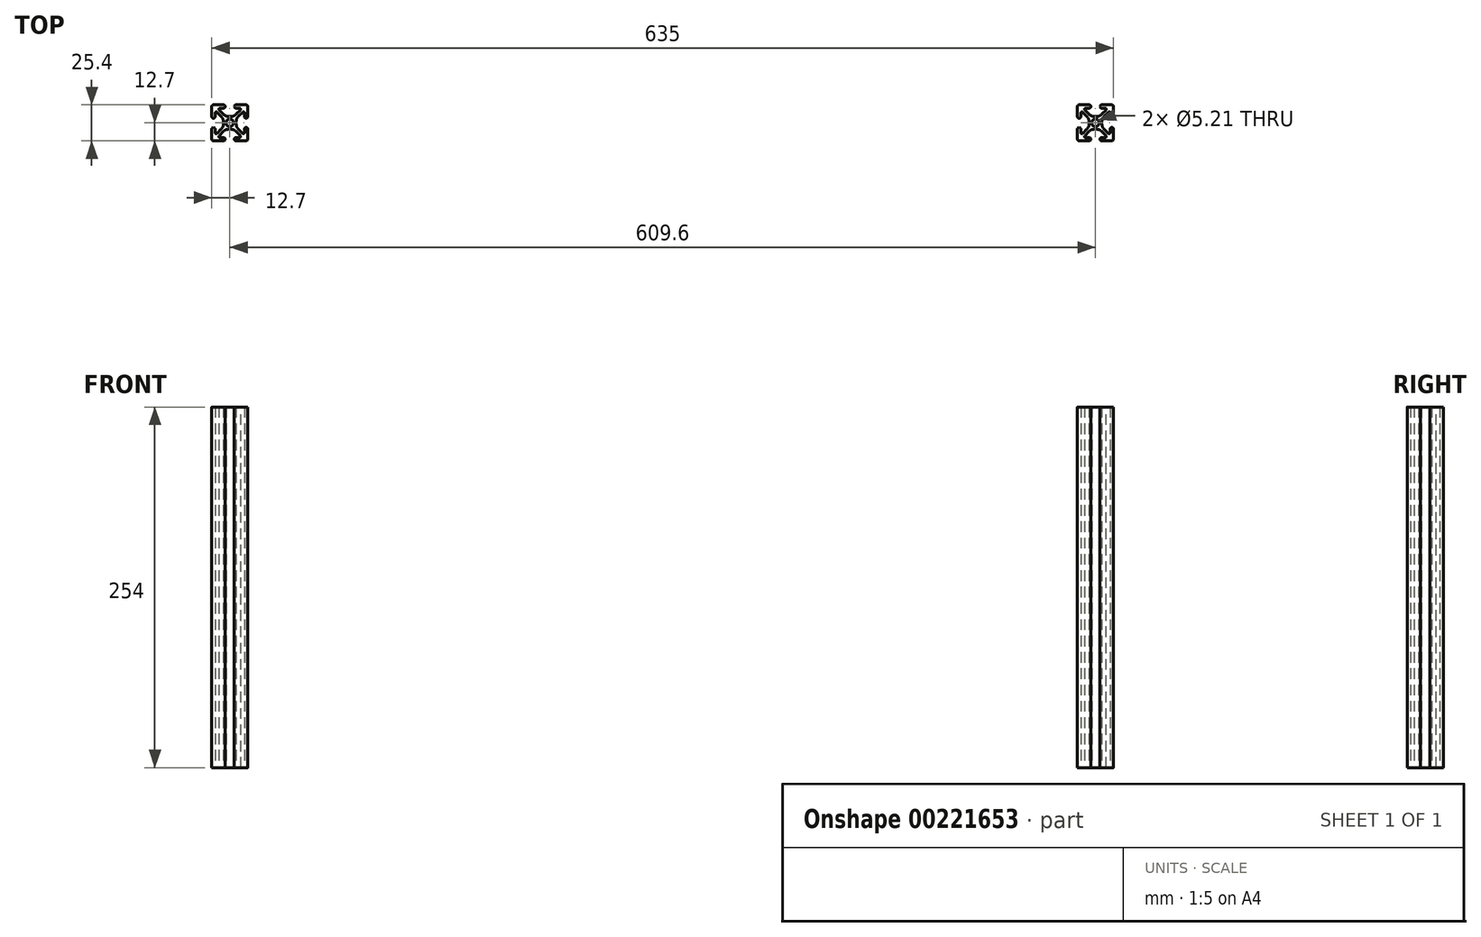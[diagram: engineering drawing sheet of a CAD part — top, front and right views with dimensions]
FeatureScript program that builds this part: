
annotation { "Feature Type Name" : "Feature", "Feature Type Description" : "" }
export const myFeature = defineFeature(function(context is Context, id is Id, definition is map)
    precondition{}
    {
        {
            var Q0;
            Q0=qCreatedBy(makeId("Top.planeOp"),FACE);
            var sketch = newSketch(context, id + "F0", { "sketchPlane" : qUnion([Q0])});
            skLineSegment(sketch, "E0.bottom", {"start": v(12.7, 12.7) * mm, "end": v(-12.7, 12.7) * mm});
            skLineSegment(sketch, "E0.top", {"start": v(12.7, -12.7) * mm, "end": v(-12.7, -12.7) * mm});
            skLineSegment(sketch, "E0.left", {"start": v(12.7, 12.7) * mm, "end": v(12.7, -12.7) * mm});
            skLineSegment(sketch, "E0.right", {"start": v(-12.7, 12.7) * mm, "end": v(-12.7, -12.7) * mm});
            skPoint(sketch, "E0.middle", {"position": v(0, 0) * mm});
            skCircle(sketch, "E1", {"center": v(0, 0) * mm, "radius": 2.6 * mm});
            skLineSegment(sketch, "E2", {"start": v(-12.7, 12.7) * mm, "end": v(12.7, -12.7) * mm, "construction": true});
            skLineSegment(sketch, "E3", {"start": v(0, 12.7) * mm, "end": v(0, -12.7) * mm, "construction": true});
            skLineSegment(sketch, "E4", {"start": v(-12.7, -12.7) * mm, "end": v(12.7, 12.7) * mm, "construction": true});
            skLineSegment(sketch, "E5", {"start": v(-8.78, 10.34) * mm, "end": v(-2.95, 4.5) * mm});
            skLineSegment(sketch, "E6.MirrorCS", {"start": v(8.78, 10.34) * mm, "end": v(2.95, 4.5) * mm});
            skLineSegment(sketch, "E7", {"start": v(-2.95, 4.5) * mm, "end": v(2.95, 4.5) * mm});
            skLineSegment(sketch, "E8.bottom", {"start": v(-3.24, 14.9) * mm, "end": v(3.24, 14.9) * mm});
            skLineSegment(sketch, "E8.left", {"start": v(-3.24, 14.9) * mm, "end": v(-3.24, 10.34) * mm});
            skLineSegment(sketch, "E8.right", {"start": v(3.24, 14.9) * mm, "end": v(3.24, 10.34) * mm});
            skLineSegment(sketch, "E9", {"start": v(-8.78, 10.34) * mm, "end": v(-3.24, 10.34) * mm});
            skLineSegment(sketch, "E10", {"start": v(3.24, 10.34) * mm, "end": v(8.78, 10.34) * mm});
            skLineSegment(sketch, "E11.MirrorCS", {"start": v(-10.34, 8.78) * mm, "end": v(-4.5, 2.95) * mm});
            skLineSegment(sketch, "E12.MirrorCS", {"start": v(-10.34, 8.78) * mm, "end": v(-10.34, 3.24) * mm});
            skLineSegment(sketch, "E13.MirrorCS", {"start": v(-14.9, 3.24) * mm, "end": v(-10.34, 3.24) * mm});
            skLineSegment(sketch, "E14.MirrorCS", {"start": v(-14.9, 3.24) * mm, "end": v(-14.9, -3.24) * mm});
            skLineSegment(sketch, "E15.MirrorCS", {"start": v(-14.9, -3.24) * mm, "end": v(-10.34, -3.24) * mm});
            skLineSegment(sketch, "E16.MirrorCS", {"start": v(-10.34, -3.24) * mm, "end": v(-10.34, -8.78) * mm});
            skLineSegment(sketch, "E17.MirrorCS", {"start": v(-10.34, -8.78) * mm, "end": v(-4.5, -2.95) * mm});
            skLineSegment(sketch, "E18.MirrorCS", {"start": v(-4.5, 2.95) * mm, "end": v(-4.5, -2.95) * mm});
            skLineSegment(sketch, "E19.MirrorCS", {"start": v(10.34, 8.78) * mm, "end": v(4.5, 2.95) * mm});
            skLineSegment(sketch, "E20.MirrorCS", {"start": v(4.5, -2.95) * mm, "end": v(4.5, 2.95) * mm});
            skLineSegment(sketch, "E21.MirrorCS", {"start": v(10.34, -8.78) * mm, "end": v(4.5, -2.95) * mm});
            skLineSegment(sketch, "E22.MirrorCS", {"start": v(10.34, -8.78) * mm, "end": v(10.34, -3.24) * mm});
            skLineSegment(sketch, "E23.MirrorCS", {"start": v(14.9, -3.24) * mm, "end": v(10.34, -3.24) * mm});
            skLineSegment(sketch, "E24.MirrorCS", {"start": v(14.9, -3.24) * mm, "end": v(14.9, 3.24) * mm});
            skLineSegment(sketch, "E25.MirrorCS", {"start": v(14.9, 3.24) * mm, "end": v(10.34, 3.24) * mm});
            skLineSegment(sketch, "E26.MirrorCS", {"start": v(10.34, 3.24) * mm, "end": v(10.34, 8.78) * mm});
            skLineSegment(sketch, "E27", {"start": v(-12.7, 0) * mm, "end": v(12.7, 0) * mm, "construction": true});
            skLineSegment(sketch, "E28.MirrorCS", {"start": v(-8.78, -10.34) * mm, "end": v(-2.95, -4.5) * mm});
            skLineSegment(sketch, "E29.MirrorCS", {"start": v(-8.78, -10.34) * mm, "end": v(-3.24, -10.34) * mm});
            skLineSegment(sketch, "E30.MirrorCS", {"start": v(-3.24, -14.9) * mm, "end": v(-3.24, -10.34) * mm});
            skLineSegment(sketch, "E31.MirrorCS", {"start": v(-3.24, -14.9) * mm, "end": v(3.24, -14.9) * mm});
            skLineSegment(sketch, "E32.MirrorCS", {"start": v(3.24, -14.9) * mm, "end": v(3.24, -10.34) * mm});
            skLineSegment(sketch, "E33.MirrorCS", {"start": v(3.24, -10.34) * mm, "end": v(8.78, -10.34) * mm});
            skLineSegment(sketch, "E34.MirrorCS", {"start": v(8.78, -10.34) * mm, "end": v(2.95, -4.5) * mm});
            skLineSegment(sketch, "E35.MirrorCS", {"start": v(-2.95, -4.5) * mm, "end": v(2.95, -4.5) * mm});
            skSolve(sketch);
        }
        {
            var Q0;
            Q0=makeQuery(id+"F0.imprint","IMPRINT",FACE,{"disambiguationData":[TD([[makeQuery(id+"F0.imprint","IMPRINT",EDGE,{"derivedFrom":sQuery(id+"F0.wireOp",EDGE,"E1")}),-1.0]])]});
            extrude(context, id + "F1", {"entities" : qUnion([Q0]), "depth" : 254 * mm});
        }
        {
            var Q0;
            Q0=makeQuery(id+"F1.opExtrude","SWEPT_EDGE",EDGE,{"disambiguationData":[OSD([sQuery(id+"F0.wireOp",EDGE,"E0.bottom"),sQuery(id+"F0.wireOp",EDGE,"E8.right")])]});
            var Q1;
            Q1=makeQuery(id+"F1.opExtrude","SWEPT_EDGE",EDGE,{"disambiguationData":[OSD([sQuery(id+"F0.wireOp",EDGE,"E8.right"),sQuery(id+"F0.wireOp",EDGE,"E10")])]});
            var Q2;
            Q2=makeQuery(id+"F1.opExtrude","SWEPT_EDGE",EDGE,{"disambiguationData":[OSD([sQuery(id+"F0.wireOp",EDGE,"E0.bottom"),sQuery(id+"F0.wireOp",EDGE,"E8.left")])]});
            var Q3;
            Q3=makeQuery(id+"F1.opExtrude","SWEPT_EDGE",EDGE,{"disambiguationData":[OSD([sQuery(id+"F0.wireOp",EDGE,"E0.right"),sQuery(id+"F0.wireOp",EDGE,"E13.MirrorCS")])]});
            var Q4;
            Q4=makeQuery(id+"F1.opExtrude","SWEPT_EDGE",EDGE,{"disambiguationData":[OSD([sQuery(id+"F0.wireOp",EDGE,"E8.left"),sQuery(id+"F0.wireOp",EDGE,"E9")])]});
            var Q5;
            Q5=makeQuery(id+"F1.opExtrude","SWEPT_EDGE",EDGE,{"disambiguationData":[OSD([sQuery(id+"F0.wireOp",EDGE,"E12.MirrorCS"),sQuery(id+"F0.wireOp",EDGE,"E13.MirrorCS")])]});
            var Q6;
            Q6=makeQuery(id+"F1.opExtrude","SWEPT_EDGE",EDGE,{"disambiguationData":[OSD([sQuery(id+"F0.wireOp",EDGE,"E0.left"),sQuery(id+"F0.wireOp",EDGE,"E25.MirrorCS")])]});
            var Q7;
            Q7=makeQuery(id+"F1.opExtrude","SWEPT_EDGE",EDGE,{"disambiguationData":[OSD([sQuery(id+"F0.wireOp",EDGE,"E25.MirrorCS"),sQuery(id+"F0.wireOp",EDGE,"E26.MirrorCS")])]});
            var Q8;
            Q8=makeQuery(id+"F1.opExtrude","SWEPT_EDGE",EDGE,{"disambiguationData":[OSD([sQuery(id+"F0.wireOp",EDGE,"E0.left"),sQuery(id+"F0.wireOp",EDGE,"E23.MirrorCS")])]});
            var Q9;
            Q9=makeQuery(id+"F1.opExtrude","SWEPT_EDGE",EDGE,{"disambiguationData":[OSD([sQuery(id+"F0.wireOp",EDGE,"E22.MirrorCS"),sQuery(id+"F0.wireOp",EDGE,"E23.MirrorCS")])]});
            var Q10;
            Q10=makeQuery(id+"F1.opExtrude","SWEPT_EDGE",EDGE,{"disambiguationData":[OSD([sQuery(id+"F0.wireOp",EDGE,"E32.MirrorCS"),sQuery(id+"F0.wireOp",EDGE,"E33.MirrorCS")])]});
            var Q11;
            Q11=makeQuery(id+"F1.opExtrude","SWEPT_EDGE",EDGE,{"disambiguationData":[OSD([sQuery(id+"F0.wireOp",EDGE,"E29.MirrorCS"),sQuery(id+"F0.wireOp",EDGE,"E30.MirrorCS")])]});
            var Q12;
            Q12=makeQuery(id+"F1.opExtrude","SWEPT_EDGE",EDGE,{"disambiguationData":[OSD([sQuery(id+"F0.wireOp",EDGE,"E15.MirrorCS"),sQuery(id+"F0.wireOp",EDGE,"E16.MirrorCS")])]});
            var Q13;
            Q13=makeQuery(id+"F1.opExtrude","SWEPT_EDGE",EDGE,{"disambiguationData":[OSD([sQuery(id+"F0.wireOp",EDGE,"E0.right"),sQuery(id+"F0.wireOp",EDGE,"E15.MirrorCS")])]});
            var Q14;
            Q14=makeQuery(id+"F1.opExtrude","SWEPT_EDGE",EDGE,{"disambiguationData":[OSD([sQuery(id+"F0.wireOp",EDGE,"E0.top"),sQuery(id+"F0.wireOp",EDGE,"E30.MirrorCS")])]});
            var Q15;
            Q15=makeQuery(id+"F1.opExtrude","SWEPT_EDGE",EDGE,{"disambiguationData":[OSD([sQuery(id+"F0.wireOp",EDGE,"E0.top"),sQuery(id+"F0.wireOp",EDGE,"E32.MirrorCS")])]});
            fillet(context, id + "F2", {"entities" : qUnion([Q0, Q1, Q2, Q3, Q4, Q5, Q6, Q7, Q8, Q9, Q10, Q11, Q12, Q13, Q14, Q15]), "radius" : 1.18 * mm, "tangentPropagation" : true, "allowEdgeOverflow" : false});
        }
        {
            var Q0;
            Q0=makeQuery(id+"F1.opExtrude","SWEPT_EDGE",EDGE,{"disambiguationData":[OSD([sQuery(id+"F0.wireOp",EDGE,"E6.MirrorCS"),sQuery(id+"F0.wireOp",EDGE,"E7")])]});
            var Q1;
            Q1=makeQuery(id+"F1.opExtrude","SWEPT_EDGE",EDGE,{"disambiguationData":[OSD([sQuery(id+"F0.wireOp",EDGE,"E5"),sQuery(id+"F0.wireOp",EDGE,"E7")])]});
            var Q2;
            Q2=makeQuery(id+"F1.opExtrude","SWEPT_EDGE",EDGE,{"disambiguationData":[OSD([sQuery(id+"F0.wireOp",EDGE,"E20.MirrorCS"),sQuery(id+"F0.wireOp",EDGE,"E21.MirrorCS")])]});
            var Q3;
            Q3=makeQuery(id+"F1.opExtrude","SWEPT_EDGE",EDGE,{"disambiguationData":[OSD([sQuery(id+"F0.wireOp",EDGE,"E19.MirrorCS"),sQuery(id+"F0.wireOp",EDGE,"E20.MirrorCS")])]});
            var Q4;
            Q4=makeQuery(id+"F1.opExtrude","SWEPT_EDGE",EDGE,{"disambiguationData":[OSD([sQuery(id+"F0.wireOp",EDGE,"E34.MirrorCS"),sQuery(id+"F0.wireOp",EDGE,"E35.MirrorCS")])]});
            var Q5;
            Q5=makeQuery(id+"F1.opExtrude","SWEPT_EDGE",EDGE,{"disambiguationData":[OSD([sQuery(id+"F0.wireOp",EDGE,"E28.MirrorCS"),sQuery(id+"F0.wireOp",EDGE,"E35.MirrorCS")])]});
            var Q6;
            Q6=makeQuery(id+"F1.opExtrude","SWEPT_EDGE",EDGE,{"disambiguationData":[OSD([sQuery(id+"F0.wireOp",EDGE,"E17.MirrorCS"),sQuery(id+"F0.wireOp",EDGE,"E18.MirrorCS")])]});
            var Q7;
            Q7=makeQuery(id+"F1.opExtrude","SWEPT_EDGE",EDGE,{"disambiguationData":[OSD([sQuery(id+"F0.wireOp",EDGE,"E11.MirrorCS"),sQuery(id+"F0.wireOp",EDGE,"E18.MirrorCS")])]});
            fillet(context, id + "F3", {"entities" : qUnion([Q0, Q1, Q2, Q3, Q4, Q5, Q6, Q7]), "radius" : 5.08 * mm, "tangentPropagation" : true, "allowEdgeOverflow" : false});
        }
        {
            var Q0;
            Q0=makeQuery(id+"F1.opExtrude","SWEPT_EDGE",EDGE,{"disambiguationData":[OSD([sQuery(id+"F0.wireOp",EDGE,"E6.MirrorCS"),sQuery(id+"F0.wireOp",EDGE,"E10")])]});
            var Q1;
            Q1=makeQuery(id+"F1.opExtrude","SWEPT_EDGE",EDGE,{"disambiguationData":[OSD([sQuery(id+"F0.wireOp",EDGE,"E5"),sQuery(id+"F0.wireOp",EDGE,"E9")])]});
            var Q2;
            Q2=makeQuery(id+"F1.opExtrude","SWEPT_EDGE",EDGE,{"disambiguationData":[OSD([sQuery(id+"F0.wireOp",EDGE,"E11.MirrorCS"),sQuery(id+"F0.wireOp",EDGE,"E12.MirrorCS")])]});
            var Q3;
            Q3=makeQuery(id+"F1.opExtrude","SWEPT_EDGE",EDGE,{"disambiguationData":[OSD([sQuery(id+"F0.wireOp",EDGE,"E16.MirrorCS"),sQuery(id+"F0.wireOp",EDGE,"E17.MirrorCS")])]});
            var Q4;
            Q4=makeQuery(id+"F1.opExtrude","SWEPT_EDGE",EDGE,{"disambiguationData":[OSD([sQuery(id+"F0.wireOp",EDGE,"E28.MirrorCS"),sQuery(id+"F0.wireOp",EDGE,"E29.MirrorCS")])]});
            var Q5;
            Q5=makeQuery(id+"F1.opExtrude","SWEPT_EDGE",EDGE,{"disambiguationData":[OSD([sQuery(id+"F0.wireOp",EDGE,"E33.MirrorCS"),sQuery(id+"F0.wireOp",EDGE,"E34.MirrorCS")])]});
            var Q6;
            Q6=makeQuery(id+"F1.opExtrude","SWEPT_EDGE",EDGE,{"disambiguationData":[OSD([sQuery(id+"F0.wireOp",EDGE,"E21.MirrorCS"),sQuery(id+"F0.wireOp",EDGE,"E22.MirrorCS")])]});
            var Q7;
            Q7=makeQuery(id+"F1.opExtrude","SWEPT_EDGE",EDGE,{"disambiguationData":[OSD([sQuery(id+"F0.wireOp",EDGE,"E19.MirrorCS"),sQuery(id+"F0.wireOp",EDGE,"E26.MirrorCS")])]});
            fillet(context, id + "F4", {"entities" : qUnion([Q0, Q1, Q2, Q3, Q4, Q5, Q6, Q7]), "radius" : 0.76 * mm, "tangentPropagation" : true, "allowEdgeOverflow" : false});
        }
        {
            var Q0;
            Q0=makeQuery(id+"F1.opExtrude","SWEPT_EDGE",EDGE,{"disambiguationData":[OSD([sQuery(id+"F0.wireOp",EDGE,"E0.top"),sQuery(id+"F0.wireOp",EDGE,"E0.right")])]});
            var Q1;
            Q1=makeQuery(id+"F1.opExtrude","SWEPT_EDGE",EDGE,{"disambiguationData":[OSD([sQuery(id+"F0.wireOp",EDGE,"E0.top"),sQuery(id+"F0.wireOp",EDGE,"E0.left")])]});
            var Q2;
            Q2=makeQuery(id+"F1.opExtrude","SWEPT_EDGE",EDGE,{"disambiguationData":[OSD([sQuery(id+"F0.wireOp",EDGE,"E0.bottom"),sQuery(id+"F0.wireOp",EDGE,"E0.left")])]});
            var Q3;
            Q3=makeQuery(id+"F1.opExtrude","SWEPT_EDGE",EDGE,{"disambiguationData":[OSD([sQuery(id+"F0.wireOp",EDGE,"E0.bottom"),sQuery(id+"F0.wireOp",EDGE,"E0.right")])]});
            fillet(context, id + "F5", {"entities" : qUnion([Q0, Q1, Q2, Q3]), "radius" : 1.27 * mm, "tangentPropagation" : true, "allowEdgeOverflow" : false});
        }
        {
            var Q0;
            Q0=makeQuery(id+"F1.opExtrude","SWEPT_BODY",BODY,{"disambiguationData":[OSD([sQuery(id+"F0.wireOp",EDGE,"E0.bottom"),sQuery(id+"F0.wireOp",EDGE,"E0.top"),sQuery(id+"F0.wireOp",EDGE,"E0.left"),sQuery(id+"F0.wireOp",EDGE,"E0.right"),sQuery(id+"F0.wireOp",EDGE,"E1"),sQuery(id+"F0.wireOp",EDGE,"E5"),sQuery(id+"F0.wireOp",EDGE,"E6.MirrorCS"),sQuery(id+"F0.wireOp",EDGE,"E7"),sQuery(id+"F0.wireOp",EDGE,"E8.left"),sQuery(id+"F0.wireOp",EDGE,"E8.right"),sQuery(id+"F0.wireOp",EDGE,"E9"),sQuery(id+"F0.wireOp",EDGE,"E10"),sQuery(id+"F0.wireOp",EDGE,"E11.MirrorCS"),sQuery(id+"F0.wireOp",EDGE,"E12.MirrorCS"),sQuery(id+"F0.wireOp",EDGE,"E13.MirrorCS"),sQuery(id+"F0.wireOp",EDGE,"E15.MirrorCS"),sQuery(id+"F0.wireOp",EDGE,"E16.MirrorCS"),sQuery(id+"F0.wireOp",EDGE,"E17.MirrorCS"),sQuery(id+"F0.wireOp",EDGE,"E18.MirrorCS"),sQuery(id+"F0.wireOp",EDGE,"E19.MirrorCS"),sQuery(id+"F0.wireOp",EDGE,"E20.MirrorCS"),sQuery(id+"F0.wireOp",EDGE,"E21.MirrorCS"),sQuery(id+"F0.wireOp",EDGE,"E22.MirrorCS"),sQuery(id+"F0.wireOp",EDGE,"E23.MirrorCS"),sQuery(id+"F0.wireOp",EDGE,"E25.MirrorCS"),sQuery(id+"F0.wireOp",EDGE,"E26.MirrorCS"),sQuery(id+"F0.wireOp",EDGE,"E28.MirrorCS"),sQuery(id+"F0.wireOp",EDGE,"E29.MirrorCS"),sQuery(id+"F0.wireOp",EDGE,"E30.MirrorCS"),sQuery(id+"F0.wireOp",EDGE,"E32.MirrorCS"),sQuery(id+"F0.wireOp",EDGE,"E33.MirrorCS"),sQuery(id+"F0.wireOp",EDGE,"E34.MirrorCS"),sQuery(id+"F0.wireOp",EDGE,"E35.MirrorCS")])]});
            transform(context, id + "F6", {"entities" : qUnion([Q0]), "transformType" : TransformType.TRANSLATION_3D, "dx" : 609.6 * mm, "dy" : 0 * mm, "dz" : 0 * mm, "makeCopy" : true});
        }
    });
